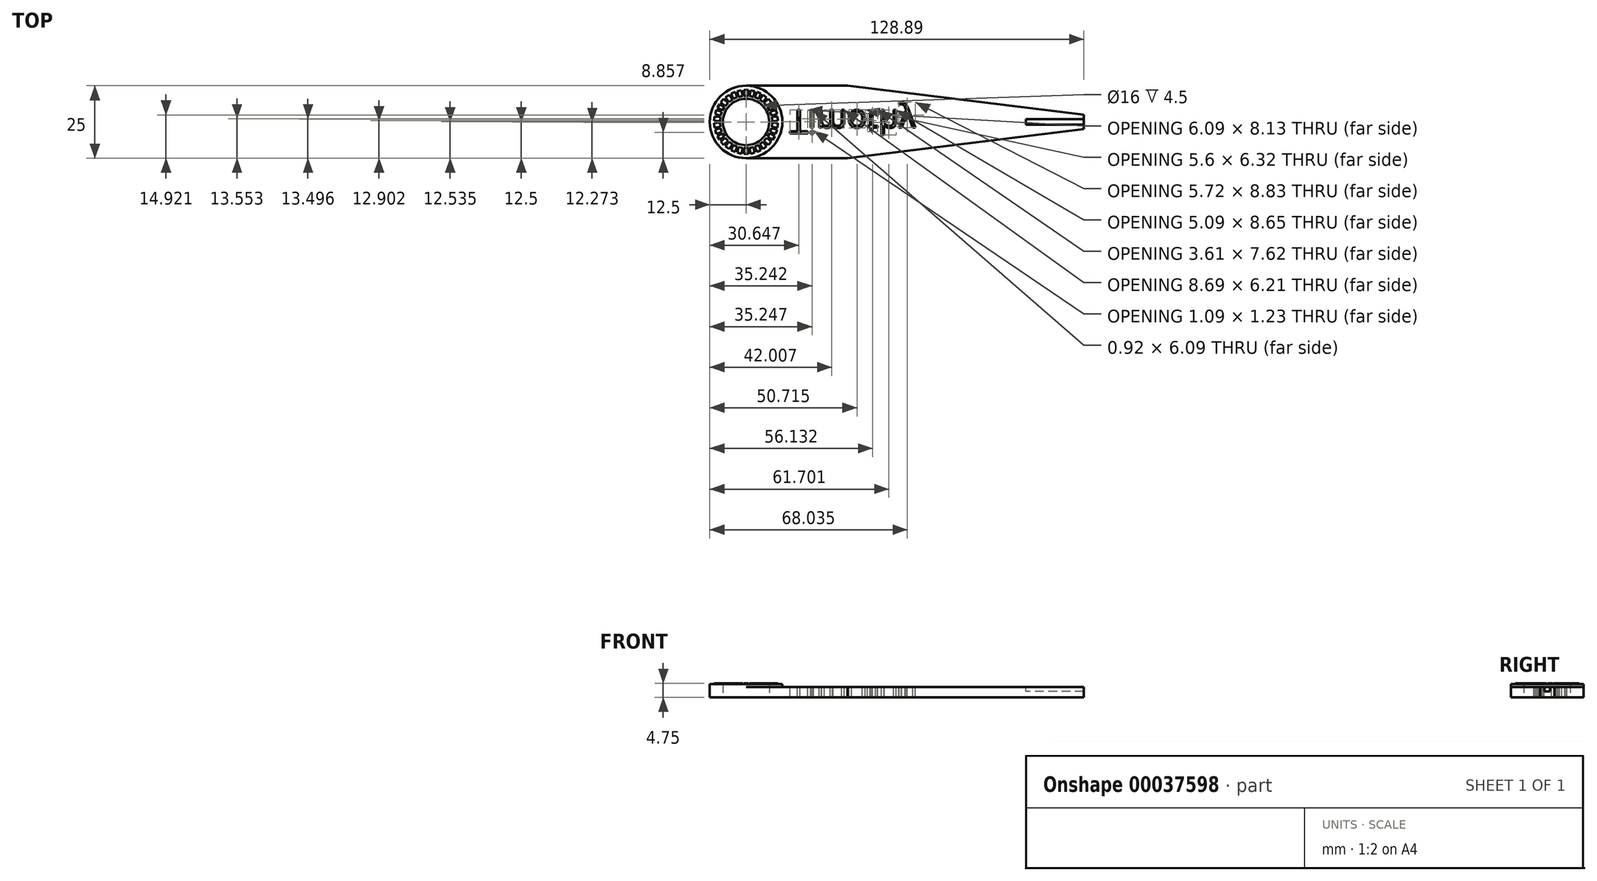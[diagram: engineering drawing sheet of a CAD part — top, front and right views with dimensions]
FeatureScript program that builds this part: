
annotation { "Feature Type Name" : "Feature", "Feature Type Description" : "" }
export const myFeature = defineFeature(function(context is Context, id is Id, definition is map)
    precondition{}
    {
        {
            var Q0;
            Q0=qCreatedBy(makeId("Top.planeOp"),FACE);
            var sketch = newSketch(context, id + "F0", { "sketchPlane" : qUnion([Q0])});
            skArc(sketch, "E0", {"start": v(0, 12.5) * mm, "mid": v(-12.5, 0) * mm, "end": v(0, -12.5) * mm});
            skCircle(sketch, "E1", {"center": v(0, 0) * mm, "radius": 8 * mm});
            skLineSegment(sketch, "E2", {"start": v(0, 12.5) * mm, "end": v(35, 12.5) * mm});
            skLineSegment(sketch, "E3", {"start": v(0, 0) * mm, "end": v(47.85, 0) * mm, "construction": true});
            skLineSegment(sketch, "E4", {"start": v(35, 12.5) * mm, "end": v(116.39, 2.5) * mm});
            skLineSegment(sketch, "E5", {"start": v(35, 12.5) * mm, "end": v(69.16, 12.5) * mm, "construction": true});
            skLineSegment(sketch, "E6.MirrorCS", {"start": v(0, -12.5) * mm, "end": v(35, -12.5) * mm});
            skLineSegment(sketch, "E7.MirrorCS", {"start": v(35, -12.5) * mm, "end": v(116.39, -2.5) * mm});
            skLineSegment(sketch, "E8", {"start": v(116.39, 2.5) * mm, "end": v(116.39, -2.5) * mm});
            skSolve(sketch);
        }
        {
            var Q0;
            Q0 = qSketchRegion(id + "F0", true);
            extrude(context, id + "F1", {"entities" : qUnion([Q0]), "depth" : 3.5 * mm});
        }
        {
            var Q0;
            Q0=makeQuery(id+"F1.opExtrude","CAP_FACE",FACE,{"disambiguationData":[OSD([sQuery(id+"F0.wireOp",EDGE,"E0"),sQuery(id+"F0.wireOp",EDGE,"E1"),sQuery(id+"F0.wireOp",EDGE,"E2"),sQuery(id+"F0.wireOp",EDGE,"E4"),sQuery(id+"F0.wireOp",EDGE,"E6.MirrorCS"),sQuery(id+"F0.wireOp",EDGE,"E7.MirrorCS"),sQuery(id+"F0.wireOp",EDGE,"E8")])],"isStart":false});
            var sketch = newSketch(context, id + "F2", { "sketchPlane" : qUnion([Q0])});
            skCircle(sketch, "E9", {"center": v(0, 0) * mm, "radius": 8 * mm});
            skCircle(sketch, "E10", {"center": v(0, 0) * mm, "radius": 12.5 * mm});
            skSolve(sketch);
        }
        {
            var Q0;
            Q0 = qSketchRegion(id + "F2", true);
            extrude(context, id + "F3", {"entities" : qUnion([Q0]), "operationType" : NewBodyOperationType.ADD, "depth" : 1 * mm});
        }
        {
            var Q0;
            Q0=makeQuery(id+"F3.opExtrude","CAP_FACE",FACE,{"disambiguationData":[OSD([sQuery(id+"F2.wireOp",EDGE,"E9"),sQuery(id+"F2.wireOp",EDGE,"E10")])],"isStart":false});
            var sketch = newSketch(context, id + "F4", { "sketchPlane" : qUnion([Q0])});
            skLineSegment(sketch, "E11.bottom", {"start": v(-0.75, 11) * mm, "end": v(0.75, 11) * mm});
            skLineSegment(sketch, "E11.top", {"start": v(-0.75, 9) * mm, "end": v(0.75, 9) * mm});
            skLineSegment(sketch, "E11.left", {"start": v(-0.75, 11) * mm, "end": v(-0.75, 9) * mm});
            skLineSegment(sketch, "E11.right", {"start": v(0.75, 11) * mm, "end": v(0.75, 9) * mm});
            skLineSegment(sketch, "E12.1.0", {"start": v(-2.6, 8.65) * mm, "end": v(-1.14, 8.96) * mm});
            skLineSegment(sketch, "E12.1.1", {"start": v(-3.02, 10.6) * mm, "end": v(-2.6, 8.65) * mm});
            skLineSegment(sketch, "E12.1.2", {"start": v(-3.02, 10.6) * mm, "end": v(-1.55, 10.92) * mm});
            skLineSegment(sketch, "E12.1.3", {"start": v(-1.55, 10.92) * mm, "end": v(-1.14, 8.96) * mm});
            skLineSegment(sketch, "E12.2.0", {"start": v(-4.35, 7.92) * mm, "end": v(-2.98, 8.53) * mm});
            skLineSegment(sketch, "E12.2.1", {"start": v(-5.16, 9.74) * mm, "end": v(-4.35, 7.92) * mm});
            skLineSegment(sketch, "E12.2.2", {"start": v(-5.16, 9.74) * mm, "end": v(-3.79, 10.35) * mm});
            skLineSegment(sketch, "E12.2.3", {"start": v(-3.79, 10.35) * mm, "end": v(-2.98, 8.53) * mm});
            skLineSegment(sketch, "E12.3.0", {"start": v(-5.9, 6.84) * mm, "end": v(-4.68, 7.72) * mm});
            skLineSegment(sketch, "E12.3.1", {"start": v(-7.07, 8.46) * mm, "end": v(-5.9, 6.84) * mm});
            skLineSegment(sketch, "E12.3.2", {"start": v(-7.07, 8.46) * mm, "end": v(-5.86, 9.34) * mm});
            skLineSegment(sketch, "E12.3.3", {"start": v(-5.86, 9.34) * mm, "end": v(-4.68, 7.72) * mm});
            skLineSegment(sketch, "E12.4.0", {"start": v(-7.2, 5.46) * mm, "end": v(-6.19, 6.58) * mm});
            skLineSegment(sketch, "E12.4.1", {"start": v(-8.68, 6.8) * mm, "end": v(-7.2, 5.46) * mm});
            skLineSegment(sketch, "E12.4.2", {"start": v(-8.68, 6.8) * mm, "end": v(-7.67, 7.92) * mm});
            skLineSegment(sketch, "E12.4.3", {"start": v(-7.67, 7.92) * mm, "end": v(-6.19, 6.58) * mm});
            skLineSegment(sketch, "E12.5.0", {"start": v(-8.17, 3.85) * mm, "end": v(-7.42, 5.15) * mm});
            skLineSegment(sketch, "E12.5.1", {"start": v(-9.9, 4.85) * mm, "end": v(-8.17, 3.85) * mm});
            skLineSegment(sketch, "E12.5.2", {"start": v(-9.9, 4.85) * mm, "end": v(-9.15, 6.15) * mm});
            skLineSegment(sketch, "E12.5.3", {"start": v(-9.15, 6.15) * mm, "end": v(-7.42, 5.15) * mm});
            skLineSegment(sketch, "E12.6.0", {"start": v(-8.8, 2.07) * mm, "end": v(-8.33, 3.5) * mm});
            skLineSegment(sketch, "E12.6.1", {"start": v(-10.7, 2.69) * mm, "end": v(-8.8, 2.07) * mm});
            skLineSegment(sketch, "E12.6.2", {"start": v(-10.7, 2.69) * mm, "end": v(-10.23, 4.11) * mm});
            skLineSegment(sketch, "E12.6.3", {"start": v(-10.23, 4.11) * mm, "end": v(-8.33, 3.5) * mm});
            skLineSegment(sketch, "E12.7.0", {"start": v(-9.03, 0.2) * mm, "end": v(-8.87, 1.69) * mm});
            skLineSegment(sketch, "E12.7.1", {"start": v(-11.02, 0.4) * mm, "end": v(-9.03, 0.2) * mm});
            skLineSegment(sketch, "E12.7.2", {"start": v(-11.02, 0.4) * mm, "end": v(-10.86, 1.9) * mm});
            skLineSegment(sketch, "E12.7.3", {"start": v(-10.86, 1.9) * mm, "end": v(-8.87, 1.69) * mm});
            skLineSegment(sketch, "E12.8.0", {"start": v(-8.87, -1.69) * mm, "end": v(-9.03, -0.2) * mm});
            skLineSegment(sketch, "E12.8.1", {"start": v(-10.86, -1.9) * mm, "end": v(-8.87, -1.69) * mm});
            skLineSegment(sketch, "E12.8.2", {"start": v(-10.86, -1.9) * mm, "end": v(-11.02, -0.4) * mm});
            skLineSegment(sketch, "E12.8.3", {"start": v(-11.02, -0.4) * mm, "end": v(-9.03, -0.2) * mm});
            skLineSegment(sketch, "E12.9.0", {"start": v(-8.33, -3.5) * mm, "end": v(-8.8, -2.07) * mm});
            skLineSegment(sketch, "E12.9.1", {"start": v(-10.23, -4.11) * mm, "end": v(-8.33, -3.5) * mm});
            skLineSegment(sketch, "E12.9.2", {"start": v(-10.23, -4.11) * mm, "end": v(-10.7, -2.69) * mm});
            skLineSegment(sketch, "E12.9.3", {"start": v(-10.7, -2.69) * mm, "end": v(-8.8, -2.07) * mm});
            skLineSegment(sketch, "E12.10.0", {"start": v(-7.42, -5.15) * mm, "end": v(-8.17, -3.85) * mm});
            skLineSegment(sketch, "E12.10.1", {"start": v(-9.15, -6.15) * mm, "end": v(-7.42, -5.15) * mm});
            skLineSegment(sketch, "E12.10.2", {"start": v(-9.15, -6.15) * mm, "end": v(-9.9, -4.85) * mm});
            skLineSegment(sketch, "E12.10.3", {"start": v(-9.9, -4.85) * mm, "end": v(-8.17, -3.85) * mm});
            skLineSegment(sketch, "E12.11.0", {"start": v(-6.19, -6.58) * mm, "end": v(-7.2, -5.46) * mm});
            skLineSegment(sketch, "E12.11.1", {"start": v(-7.67, -7.92) * mm, "end": v(-6.19, -6.58) * mm});
            skLineSegment(sketch, "E12.11.2", {"start": v(-7.67, -7.92) * mm, "end": v(-8.68, -6.8) * mm});
            skLineSegment(sketch, "E12.11.3", {"start": v(-8.68, -6.8) * mm, "end": v(-7.2, -5.46) * mm});
            skLineSegment(sketch, "E12.12.0", {"start": v(-4.68, -7.72) * mm, "end": v(-5.9, -6.84) * mm});
            skLineSegment(sketch, "E12.12.1", {"start": v(-5.86, -9.34) * mm, "end": v(-4.68, -7.72) * mm});
            skLineSegment(sketch, "E12.12.2", {"start": v(-5.86, -9.34) * mm, "end": v(-7.07, -8.46) * mm});
            skLineSegment(sketch, "E12.12.3", {"start": v(-7.07, -8.46) * mm, "end": v(-5.9, -6.84) * mm});
            skLineSegment(sketch, "E12.13.0", {"start": v(-2.98, -8.53) * mm, "end": v(-4.35, -7.92) * mm});
            skLineSegment(sketch, "E12.13.1", {"start": v(-3.79, -10.35) * mm, "end": v(-2.98, -8.53) * mm});
            skLineSegment(sketch, "E12.13.2", {"start": v(-3.79, -10.35) * mm, "end": v(-5.16, -9.74) * mm});
            skLineSegment(sketch, "E12.13.3", {"start": v(-5.16, -9.74) * mm, "end": v(-4.35, -7.92) * mm});
            skLineSegment(sketch, "E12.14.0", {"start": v(-1.14, -8.96) * mm, "end": v(-2.6, -8.65) * mm});
            skLineSegment(sketch, "E12.14.1", {"start": v(-1.55, -10.92) * mm, "end": v(-1.14, -8.96) * mm});
            skLineSegment(sketch, "E12.14.2", {"start": v(-1.55, -10.92) * mm, "end": v(-3.02, -10.6) * mm});
            skLineSegment(sketch, "E12.14.3", {"start": v(-3.02, -10.6) * mm, "end": v(-2.6, -8.65) * mm});
            skLineSegment(sketch, "E12.15.0", {"start": v(0.75, -9) * mm, "end": v(-0.75, -9) * mm});
            skLineSegment(sketch, "E12.15.1", {"start": v(0.75, -11) * mm, "end": v(0.75, -9) * mm});
            skLineSegment(sketch, "E12.15.2", {"start": v(0.75, -11) * mm, "end": v(-0.75, -11) * mm});
            skLineSegment(sketch, "E12.15.3", {"start": v(-0.75, -11) * mm, "end": v(-0.75, -9) * mm});
            skLineSegment(sketch, "E12.16.0", {"start": v(2.6, -8.65) * mm, "end": v(1.14, -8.96) * mm});
            skLineSegment(sketch, "E12.16.1", {"start": v(3.02, -10.6) * mm, "end": v(2.6, -8.65) * mm});
            skLineSegment(sketch, "E12.16.2", {"start": v(3.02, -10.6) * mm, "end": v(1.55, -10.92) * mm});
            skLineSegment(sketch, "E12.16.3", {"start": v(1.55, -10.92) * mm, "end": v(1.14, -8.96) * mm});
            skLineSegment(sketch, "E12.17.0", {"start": v(4.35, -7.92) * mm, "end": v(2.98, -8.53) * mm});
            skLineSegment(sketch, "E12.17.1", {"start": v(5.16, -9.74) * mm, "end": v(4.35, -7.92) * mm});
            skLineSegment(sketch, "E12.17.2", {"start": v(5.16, -9.74) * mm, "end": v(3.79, -10.35) * mm});
            skLineSegment(sketch, "E12.17.3", {"start": v(3.79, -10.35) * mm, "end": v(2.98, -8.53) * mm});
            skLineSegment(sketch, "E12.18.0", {"start": v(5.9, -6.84) * mm, "end": v(4.68, -7.72) * mm});
            skLineSegment(sketch, "E12.18.1", {"start": v(7.07, -8.46) * mm, "end": v(5.9, -6.84) * mm});
            skLineSegment(sketch, "E12.18.2", {"start": v(7.07, -8.46) * mm, "end": v(5.86, -9.34) * mm});
            skLineSegment(sketch, "E12.18.3", {"start": v(5.86, -9.34) * mm, "end": v(4.68, -7.72) * mm});
            skLineSegment(sketch, "E12.19.0", {"start": v(7.2, -5.46) * mm, "end": v(6.19, -6.58) * mm});
            skLineSegment(sketch, "E12.19.1", {"start": v(8.68, -6.8) * mm, "end": v(7.2, -5.46) * mm});
            skLineSegment(sketch, "E12.19.2", {"start": v(8.68, -6.8) * mm, "end": v(7.67, -7.92) * mm});
            skLineSegment(sketch, "E12.19.3", {"start": v(7.67, -7.92) * mm, "end": v(6.19, -6.58) * mm});
            skLineSegment(sketch, "E12.20.0", {"start": v(8.17, -3.85) * mm, "end": v(7.42, -5.15) * mm});
            skLineSegment(sketch, "E12.20.1", {"start": v(9.9, -4.85) * mm, "end": v(8.17, -3.85) * mm});
            skLineSegment(sketch, "E12.20.2", {"start": v(9.9, -4.85) * mm, "end": v(9.15, -6.15) * mm});
            skLineSegment(sketch, "E12.20.3", {"start": v(9.15, -6.15) * mm, "end": v(7.42, -5.15) * mm});
            skLineSegment(sketch, "E12.21.0", {"start": v(8.8, -2.07) * mm, "end": v(8.33, -3.5) * mm});
            skLineSegment(sketch, "E12.21.1", {"start": v(10.7, -2.69) * mm, "end": v(8.8, -2.07) * mm});
            skLineSegment(sketch, "E12.21.2", {"start": v(10.7, -2.69) * mm, "end": v(10.23, -4.11) * mm});
            skLineSegment(sketch, "E12.21.3", {"start": v(10.23, -4.11) * mm, "end": v(8.33, -3.5) * mm});
            skLineSegment(sketch, "E12.22.0", {"start": v(9.03, -0.2) * mm, "end": v(8.87, -1.69) * mm});
            skLineSegment(sketch, "E12.22.1", {"start": v(11.02, -0.4) * mm, "end": v(9.03, -0.2) * mm});
            skLineSegment(sketch, "E12.22.2", {"start": v(11.02, -0.4) * mm, "end": v(10.86, -1.9) * mm});
            skLineSegment(sketch, "E12.22.3", {"start": v(10.86, -1.9) * mm, "end": v(8.87, -1.69) * mm});
            skLineSegment(sketch, "E12.23.0", {"start": v(8.87, 1.69) * mm, "end": v(9.03, 0.2) * mm});
            skLineSegment(sketch, "E12.23.1", {"start": v(10.86, 1.9) * mm, "end": v(8.87, 1.69) * mm});
            skLineSegment(sketch, "E12.23.2", {"start": v(10.86, 1.9) * mm, "end": v(11.02, 0.4) * mm});
            skLineSegment(sketch, "E12.23.3", {"start": v(11.02, 0.4) * mm, "end": v(9.03, 0.2) * mm});
            skLineSegment(sketch, "E12.24.0", {"start": v(8.33, 3.5) * mm, "end": v(8.8, 2.07) * mm});
            skLineSegment(sketch, "E12.24.1", {"start": v(10.23, 4.11) * mm, "end": v(8.33, 3.5) * mm});
            skLineSegment(sketch, "E12.24.2", {"start": v(10.23, 4.11) * mm, "end": v(10.7, 2.69) * mm});
            skLineSegment(sketch, "E12.24.3", {"start": v(10.7, 2.69) * mm, "end": v(8.8, 2.07) * mm});
            skLineSegment(sketch, "E12.25.0", {"start": v(7.42, 5.15) * mm, "end": v(8.17, 3.85) * mm});
            skLineSegment(sketch, "E12.25.1", {"start": v(9.15, 6.15) * mm, "end": v(7.42, 5.15) * mm});
            skLineSegment(sketch, "E12.25.2", {"start": v(9.15, 6.15) * mm, "end": v(9.9, 4.85) * mm});
            skLineSegment(sketch, "E12.25.3", {"start": v(9.9, 4.85) * mm, "end": v(8.17, 3.85) * mm});
            skLineSegment(sketch, "E12.26.0", {"start": v(6.19, 6.58) * mm, "end": v(7.2, 5.46) * mm});
            skLineSegment(sketch, "E12.26.1", {"start": v(7.67, 7.92) * mm, "end": v(6.19, 6.58) * mm});
            skLineSegment(sketch, "E12.26.2", {"start": v(7.67, 7.92) * mm, "end": v(8.68, 6.8) * mm});
            skLineSegment(sketch, "E12.26.3", {"start": v(8.68, 6.8) * mm, "end": v(7.2, 5.46) * mm});
            skLineSegment(sketch, "E12.27.0", {"start": v(4.68, 7.72) * mm, "end": v(5.9, 6.84) * mm});
            skLineSegment(sketch, "E12.27.1", {"start": v(5.86, 9.34) * mm, "end": v(4.68, 7.72) * mm});
            skLineSegment(sketch, "E12.27.2", {"start": v(5.86, 9.34) * mm, "end": v(7.07, 8.46) * mm});
            skLineSegment(sketch, "E12.27.3", {"start": v(7.07, 8.46) * mm, "end": v(5.9, 6.84) * mm});
            skLineSegment(sketch, "E12.28.0", {"start": v(2.98, 8.53) * mm, "end": v(4.35, 7.92) * mm});
            skLineSegment(sketch, "E12.28.1", {"start": v(3.79, 10.35) * mm, "end": v(2.98, 8.53) * mm});
            skLineSegment(sketch, "E12.28.2", {"start": v(3.79, 10.35) * mm, "end": v(5.16, 9.74) * mm});
            skLineSegment(sketch, "E12.28.3", {"start": v(5.16, 9.74) * mm, "end": v(4.35, 7.92) * mm});
            skLineSegment(sketch, "E12.29.0", {"start": v(1.14, 8.96) * mm, "end": v(2.6, 8.65) * mm});
            skLineSegment(sketch, "E12.29.1", {"start": v(1.55, 10.92) * mm, "end": v(1.14, 8.96) * mm});
            skLineSegment(sketch, "E12.29.2", {"start": v(1.55, 10.92) * mm, "end": v(3.02, 10.6) * mm});
            skLineSegment(sketch, "E12.29.3", {"start": v(3.02, 10.6) * mm, "end": v(2.6, 8.65) * mm});
            skPoint(sketch, "E12.center", {"position": v(0, 0) * mm});
            skSolve(sketch);
        }
        {
            var Q0;
            Q0 = qSketchRegion(id + "F4", true);
            extrude(context, id + "F5", {"entities" : qUnion([Q0]), "operationType" : NewBodyOperationType.ADD, "depth" : 0.25 * mm});
        }
        {
            var Q0;
            Q0=makeQuery(id+"F1.opExtrude","CAP_FACE",FACE,{"disambiguationData":[OSD([sQuery(id+"F0.wireOp",EDGE,"E0"),sQuery(id+"F0.wireOp",EDGE,"E1"),sQuery(id+"F0.wireOp",EDGE,"E2"),sQuery(id+"F0.wireOp",EDGE,"E4"),sQuery(id+"F0.wireOp",EDGE,"E6.MirrorCS"),sQuery(id+"F0.wireOp",EDGE,"E7.MirrorCS"),sQuery(id+"F0.wireOp",EDGE,"E8")])],"isStart":false});
            var sketch = newSketch(context, id + "F6", { "sketchPlane" : qUnion([Q0])});
            skLineSegment(sketch, "E13.bottom", {"start": v(116.39, 1) * mm, "end": v(96.39, 1) * mm});
            skLineSegment(sketch, "E13.top", {"start": v(116.39, -1) * mm, "end": v(96.39, -1) * mm});
            skLineSegment(sketch, "E13.left", {"start": v(116.39, 1) * mm, "end": v(116.39, -1) * mm});
            skLineSegment(sketch, "E13.right", {"start": v(96.39, 1) * mm, "end": v(96.39, -1) * mm});
            skSolve(sketch);
        }
        {
            var Q0;
            Q0 = qSketchRegion(id + "F6", true);
            extrude(context, id + "F7", {"entities" : qUnion([Q0]), "operationType" : NewBodyOperationType.REMOVE, "oppositeDirection" : true, "depth" : 1.5 * mm});
        }
        {
            var Q0;
            Q0=qCreatedBy(makeId("Top.planeOp"),FACE);
            var Q1;
            Q1=makeQuery(id+"F1.opExtrude","CAP_EDGE",EDGE,{"disambiguationData":[OSD([sQuery(id+"F0.wireOp",EDGE,"E2")])],"isStart":false});
            cPlane(context, id + "F8", {"entities" : qUnion([Q0, Q1]), "cplaneType" : CPlaneType.LINE_ANGLE, "offset" : 150 * mm, "angle" : 0 * degree, "width" : 150 * mm, "height" : 150 * mm});
        }
        {
            var Q0;
            Q0=qCreatedBy(id+"F8.planeOp",FACE);
            var sketch = newSketch(context, id + "F9", { "sketchPlane" : qUnion([Q0])});
            skText(sketch, "E14", { "text": "Timothy", "fontName": "OpenSans-Regular.ttf"});
            skPoint(sketch, "E15", {"position": v(15, 0) * mm});
            const initialGuessF9  = {"E14": [0.015, -0.0041, 1, 0, 0.0082]};
            skSetInitialGuess(sketch, initialGuessF9);
            skSolve(sketch);
        }
        {
            var Q0;
            Q0 = qSketchRegion(id + "F9", true);
            extrude(context, id + "F10", {"entities" : qUnion([Q0]), "operationType" : NewBodyOperationType.REMOVE, "endBound" : BoundingType.THROUGH_ALL, "depth" : 1.5 * mm});
        }
    });
